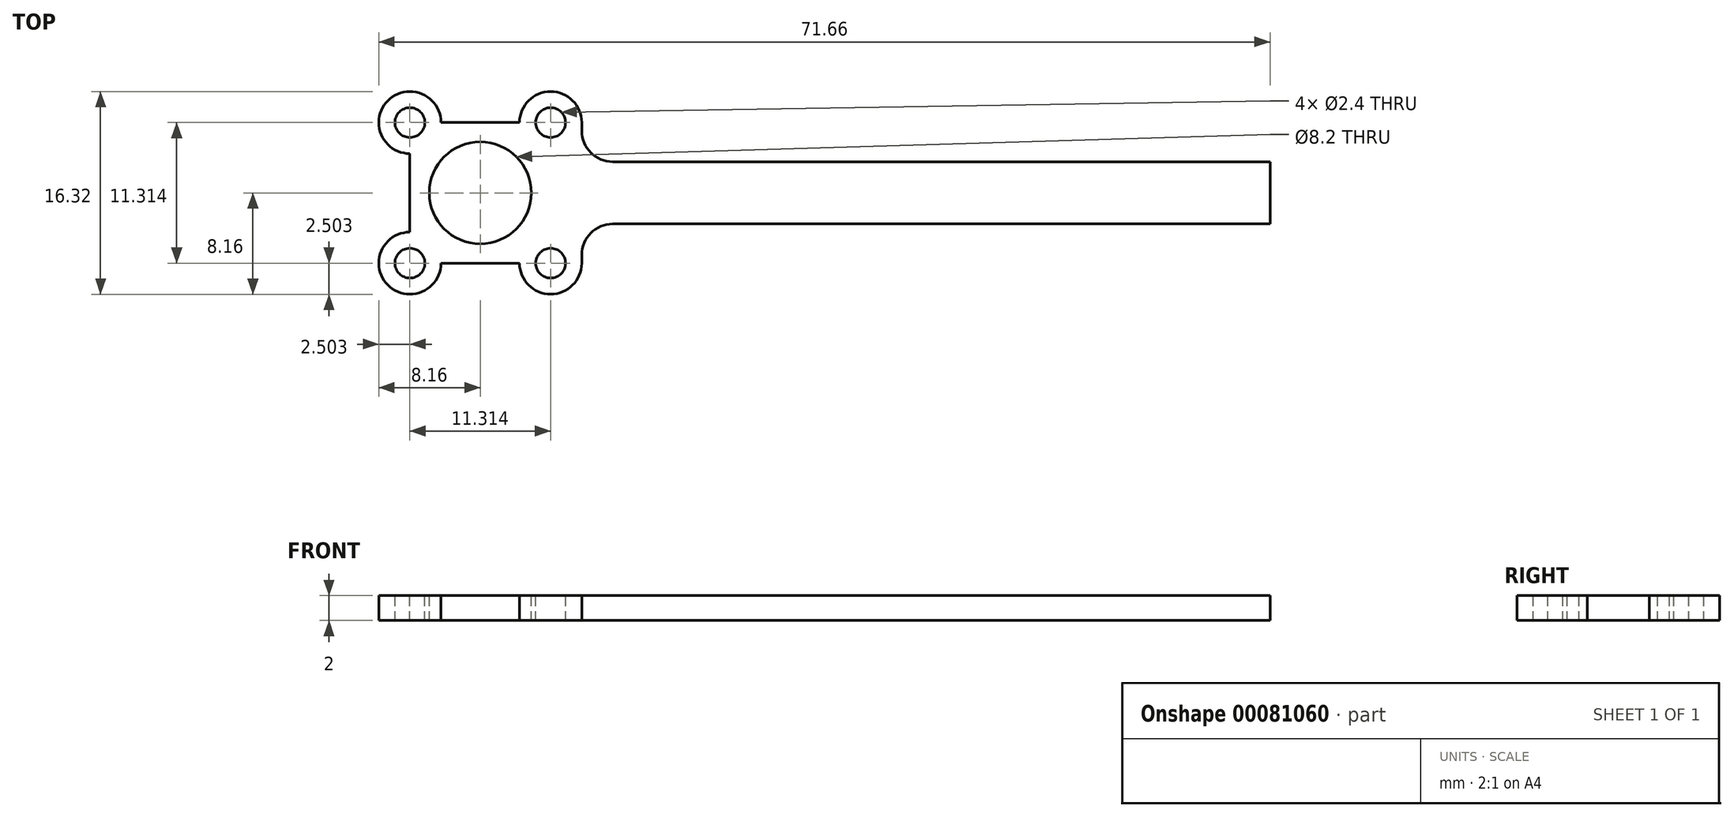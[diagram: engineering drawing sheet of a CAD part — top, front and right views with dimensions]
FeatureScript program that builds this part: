
annotation { "Feature Type Name" : "Feature", "Feature Type Description" : "" }
export const myFeature = defineFeature(function(context is Context, id is Id, definition is map)
    precondition{}
    {
        {
            var Q0;
            Q0=qCreatedBy(makeId("Top.planeOp"),FACE);
            var sketch = newSketch(context, id + "F0", { "sketchPlane" : qUnion([Q0])});
            skLineSegment(sketch, "E0.bottom", {"start": v(5.66, 5.66) * mm, "end": v(-5.66, 5.66) * mm, "construction": true});
            skLineSegment(sketch, "E0.top", {"start": v(5.66, -5.66) * mm, "end": v(-5.66, -5.66) * mm, "construction": true});
            skLineSegment(sketch, "E0.left", {"start": v(5.66, 5.66) * mm, "end": v(5.66, -5.66) * mm, "construction": true});
            skLineSegment(sketch, "E0.right", {"start": v(-5.66, 5.66) * mm, "end": v(-5.66, -5.66) * mm, "construction": true});
            skPoint(sketch, "E0.middle", {"position": v(0, 0) * mm});
            skLineSegment(sketch, "E1", {"start": v(-5.66, -5.66) * mm, "end": v(5.66, 5.66) * mm, "construction": true});
            skCircle(sketch, "E2", {"center": v(-5.66, 5.66) * mm, "radius": 1.2 * mm, "construction": true});
            skCircle(sketch, "E3", {"center": v(5.66, 5.66) * mm, "radius": 1.2 * mm, "construction": true});
            skCircle(sketch, "E4", {"center": v(-5.66, -5.66) * mm, "radius": 1.2 * mm, "construction": true});
            skCircle(sketch, "E5", {"center": v(5.66, -5.66) * mm, "radius": 1.2 * mm, "construction": true});
            skLineSegment(sketch, "E6", {"start": v(0, 0) * mm, "end": v(24.16, 0) * mm, "construction": true});
            skLineSegment(sketch, "E7", {"start": v(24.16, 6.5) * mm, "end": v(24.16, -6.5) * mm, "construction": true});
            skLineSegment(sketch, "E8", {"start": v(24.16, 6.5) * mm, "end": v(49.16, 6.5) * mm, "construction": true});
            skLineSegment(sketch, "E9", {"start": v(49.16, 6.5) * mm, "end": v(49.16, -6.5) * mm, "construction": true});
            skLineSegment(sketch, "E10", {"start": v(49.16, -6.5) * mm, "end": v(24.16, -6.5) * mm, "construction": true});
            skLineSegment(sketch, "E11", {"start": v(0, 0) * mm, "end": v(63.5, 0) * mm, "construction": true});
            skSolve(sketch);
        }
        {
            var Q0;
            Q0=qCreatedBy(makeId("Top.planeOp"),FACE);
            var sketch = newSketch(context, id + "F1", { "sketchPlane" : qUnion([Q0])});
            skLineSegment(sketch, "E12.0", {"start": v(5.66, 5.66) * mm, "end": v(-5.66, 5.66) * mm, "construction": true});
            skLineSegment(sketch, "E13.0", {"start": v(-5.66, 5.66) * mm, "end": v(-5.66, -5.66) * mm, "construction": true});
            skLineSegment(sketch, "E14.0", {"start": v(5.66, -5.66) * mm, "end": v(-5.66, -5.66) * mm, "construction": true});
            skLineSegment(sketch, "E15.0", {"start": v(5.66, 5.66) * mm, "end": v(5.66, -5.66) * mm, "construction": true});
            skCircle(sketch, "E16.0", {"center": v(-5.66, 5.66) * mm, "radius": 1.2 * mm});
            skCircle(sketch, "E17.0", {"center": v(5.66, 5.66) * mm, "radius": 1.2 * mm});
            skCircle(sketch, "E18.0", {"center": v(-5.66, -5.66) * mm, "radius": 1.2 * mm});
            skCircle(sketch, "E19.0", {"center": v(5.66, -5.66) * mm, "radius": 1.2 * mm});
            skArc(sketch, "E20", {"start": v(-3.16, 5.66) * mm, "mid": v(-7.42, 7.42) * mm, "end": v(-5.66, 3.16) * mm});
            skArc(sketch, "E21", {"start": v(-5.66, -3.16) * mm, "mid": v(-7.42, -7.42) * mm, "end": v(-3.16, -5.66) * mm});
            skArc(sketch, "E22", {"start": v(3.16, -5.66) * mm, "mid": v(7.42, -7.42) * mm, "end": v(5.66, -3.16) * mm});
            skArc(sketch, "E23", {"start": v(3.16, 5.66) * mm, "mid": v(7.42, 7.42) * mm, "end": v(5.66, 3.16) * mm});
            skLineSegment(sketch, "E24", {"start": v(-3.16, 5.66) * mm, "end": v(3.16, 5.66) * mm});
            skLineSegment(sketch, "E25", {"start": v(-5.66, 3.16) * mm, "end": v(-5.66, -3.16) * mm});
            skLineSegment(sketch, "E26", {"start": v(-3.16, -5.66) * mm, "end": v(3.16, -5.66) * mm});
            skLineSegment(sketch, "E27.bottom", {"start": v(10.66, 2.5) * mm, "end": v(63.5, 2.5) * mm});
            skLineSegment(sketch, "E27.top", {"start": v(10.66, -2.5) * mm, "end": v(63.5, -2.5) * mm});
            skLineSegment(sketch, "E27.left", {"start": v(5.66, 2.5) * mm, "end": v(5.66, -2.5) * mm, "construction": true});
            skLineSegment(sketch, "E27.right", {"start": v(63.5, 2.5) * mm, "end": v(63.5, -2.5) * mm});
            skPoint(sketch, "E28", {"position": v(5.66, 0) * mm});
            skLineSegment(sketch, "E29", {"start": v(8.16, 5.66) * mm, "end": v(8.16, 5) * mm});
            skLineSegment(sketch, "E30", {"start": v(8.16, -5) * mm, "end": v(8.16, -5.66) * mm});
            skArc(sketch, "E31.filletArc", {"start": v(8.16, 5) * mm, "mid": v(8.89, 3.23) * mm, "end": v(10.66, 2.5) * mm});
            skArc(sketch, "E32.filletArc", {"start": v(10.66, -2.5) * mm, "mid": v(8.89, -3.23) * mm, "end": v(8.16, -5) * mm});
            skCircle(sketch, "E33", {"center": v(0, 0) * mm, "radius": 4.1 * mm});
            skSolve(sketch);
        }
        {
            var Q0;
            Q0 = qSketchRegion(id + "F1", true);
            extrude(context, id + "F2", {"entities" : qUnion([Q0]), "oppositeDirection" : true, "depth" : 2 * mm});
        }
    });
